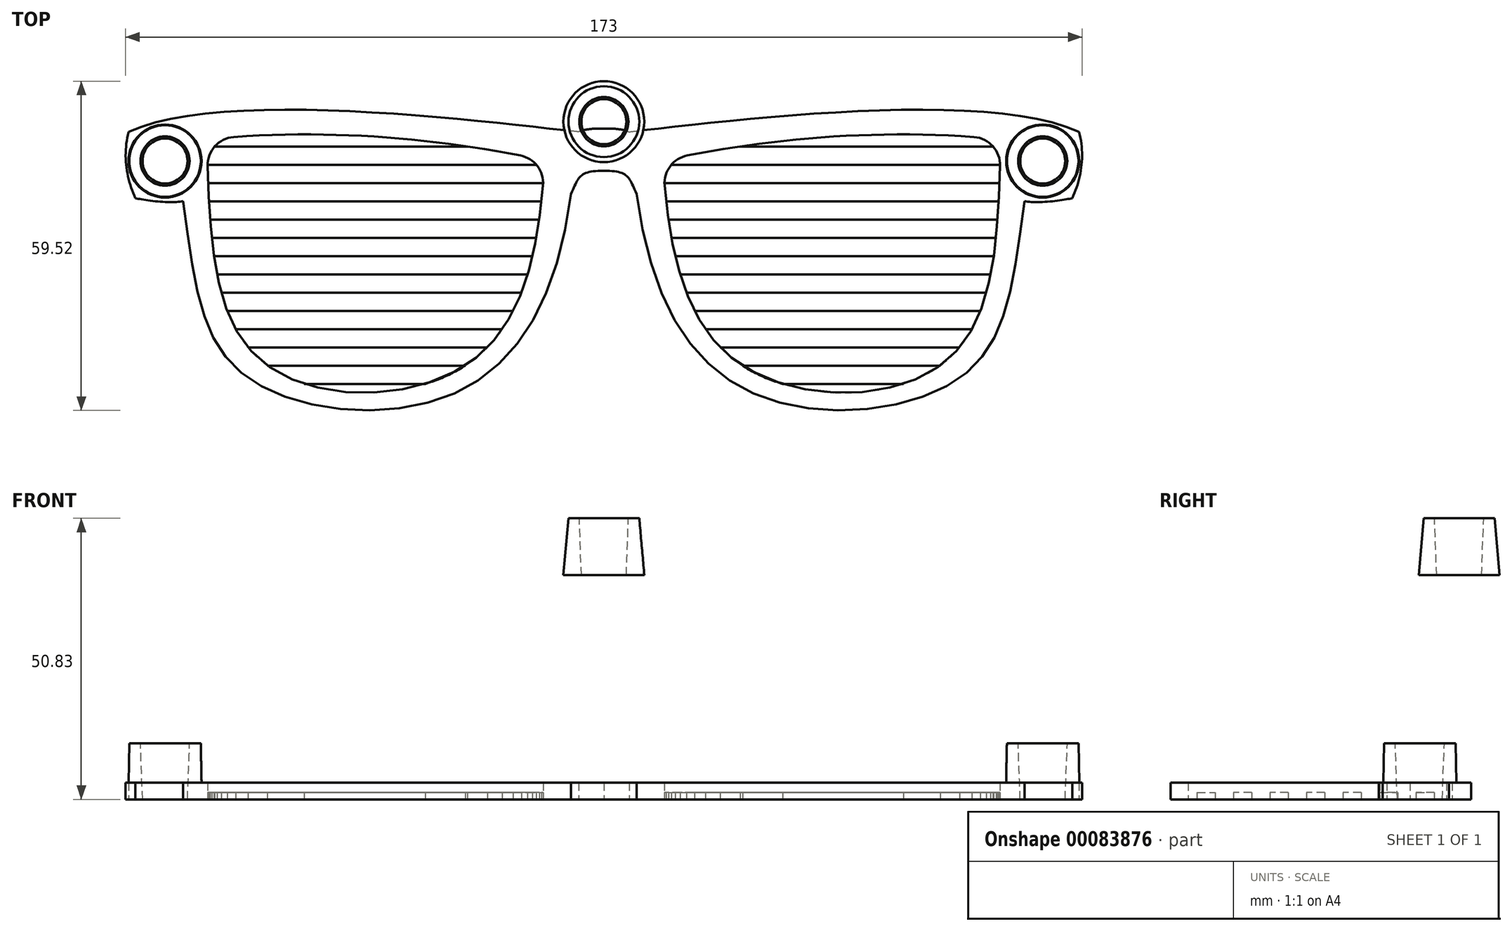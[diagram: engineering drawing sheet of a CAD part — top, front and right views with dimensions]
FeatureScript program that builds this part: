
annotation { "Feature Type Name" : "Feature", "Feature Type Description" : "" }
export const myFeature = defineFeature(function(context is Context, id is Id, definition is map)
    precondition{}
    {
        {
            var Q0;
            Q0=qCreatedBy(makeId("Top.planeOp"),FACE);
            var sketch = newSketch(context, id + "F0", { "sketchPlane" : qUnion([Q0])});
            skFitSpline(sketch, "E0", {"points": [v(0, -1.25) * mm, v(-4.57, -1.84) * mm], "startDerivative": vector(-4.29, -0.03) * mm, "endDerivative": vector(-4.84, -1.9) * mm});
            skFitSpline(sketch, "E1", {"points": [v(-4.57, -1.84) * mm, v(-85.93, -1.84) * mm], "startDerivative": vector(-55.54, 6.07) * mm, "endDerivative": vector(-50.97, -23.71) * mm});
            skFitSpline(sketch, "E2", {"points": [v(-76.11, -14.35) * mm, v(-64.79, -46.04) * mm, v(-27.62, -49.4) * mm, v(-5.92, -13.06) * mm], "startDerivative": vector(19.74, -143.66) * mm, "endDerivative": vector(20.37, 155.62) * mm});
            skFitSpline(sketch, "E3", {"points": [v(-5.92, -13.06) * mm, v(0, -8.87) * mm], "startDerivative": vector(4.13, 9.55) * mm, "endDerivative": vector(13.05, 0) * mm});
            skLineSegment(sketch, "E4", {"start": v(0, -1.25) * mm, "end": v(0, -8.87) * mm});
            skFitSpline(sketch, "E5", {"points": [v(-85.93, -1.84) * mm, v(-84.72, -13.81) * mm], "startDerivative": vector(-3.44, -12.2) * mm, "endDerivative": vector(4.98, -10.41) * mm});
            skFitSpline(sketch, "E6", {"points": [v(-84.72, -13.81) * mm, v(-76.11, -14.35) * mm], "startDerivative": vector(4.96, -1.42) * mm, "endDerivative": vector(5.45, 1.47) * mm});
            skCircle(sketch, "E7", {"center": v(-79.38, -7.12) * mm, "radius": 4.25 * mm});
            skFitSpline(sketch, "E8", {"points": [v(-10.67, -7.02) * mm, v(-24.61, -43.79) * mm, v(-62.05, -43.18) * mm, v(-71.83, -3.21) * mm], "startDerivative": vector(-7.94, -134.67) * mm, "endDerivative": vector(-5.24, 133.94) * mm});
            skFitSpline(sketch, "E9", {"points": [v(-71.83, -3.21) * mm, v(-10.67, -7.02) * mm], "startDerivative": vector(63.48, 6.5) * mm, "endDerivative": vector(56.84, -12.23) * mm});
            skSolve(sketch);
        }
        {
            var Q0;
            Q0=makeQuery(id+"F0.imprint","IMPRINT",FACE,{"disambiguationData":[TD([[makeQuery(id+"F0.imprint","IMPRINT",EDGE,{"derivedFrom":sQuery(id+"F0.wireOp",EDGE,"E0")}),1.0]])]});
            extrude(context, id + "F1", {"entities" : qUnion([Q0]), "depth" : 3.05 * mm});
        }
        {
            var Q0;
            {var subQ0=sQuery(id+"F0.wireOp",EDGE,"E9");var subQ1=sQuery(id+"F0.wireOp",EDGE,"E8");Q0=makeQuery(id+"F1.opExtrude","SWEPT_EDGE",EDGE,{"disambiguationData":[OSD([subQ1,subQ0]),TDD([makeQuery(id+"F0.imprint","INTERSECT",VERTEX,{"disambiguationData":[OD(1.0)],"derivedFrom":[subQ1,subQ0]})])]});}
            var Q1;
            {var subQ0=sQuery(id+"F0.wireOp",EDGE,"E9");var subQ1=sQuery(id+"F0.wireOp",EDGE,"E8");Q1=makeQuery(id+"F1.opExtrude","SWEPT_EDGE",EDGE,{"disambiguationData":[OSD([subQ1,subQ0]),TDD([makeQuery(id+"F0.imprint","INTERSECT",VERTEX,{"disambiguationData":[OD(0.0)],"derivedFrom":[subQ1,subQ0]})])]});}
            fillet(context, id + "F2", {"entities" : qUnion([Q0, Q1]), "radius" : 5.08 * mm, "tangentPropagation" : true, "allowEdgeOverflow" : false});
        }
        {
            var Q0;
            Q0=qCreatedBy(makeId("Top.planeOp"),FACE);
            var sketch = newSketch(context, id + "F3", { "sketchPlane" : qUnion([Q0])});
            skLineSegment(sketch, "E10.bottom", {"start": v(-72.86, -4.48) * mm, "end": v(-7.58, -4.48) * mm});
            skLineSegment(sketch, "E10.top", {"start": v(-72.86, -7.78) * mm, "end": v(-7.58, -7.78) * mm});
            skLineSegment(sketch, "E10.left", {"start": v(-72.86, -4.48) * mm, "end": v(-72.86, -7.78) * mm});
            skLineSegment(sketch, "E10.right", {"start": v(-7.58, -4.48) * mm, "end": v(-7.58, -7.78) * mm});
            skLineSegment(sketch, "E11.bottom", {"start": v(-73.3, -11.08) * mm, "end": v(-9.13, -11.08) * mm});
            skLineSegment(sketch, "E11.top", {"start": v(-73.3, -14.39) * mm, "end": v(-9.13, -14.39) * mm});
            skLineSegment(sketch, "E11.left", {"start": v(-73.3, -11.08) * mm, "end": v(-73.3, -14.39) * mm});
            skLineSegment(sketch, "E11.right", {"start": v(-9.13, -11.08) * mm, "end": v(-9.13, -14.39) * mm});
            skLineSegment(sketch, "E12.bottom", {"start": v(-10.38, -17.69) * mm, "end": v(-73, -17.69) * mm});
            skLineSegment(sketch, "E12.top", {"start": v(-10.38, -21) * mm, "end": v(-73, -21) * mm});
            skLineSegment(sketch, "E12.left", {"start": v(-10.38, -17.69) * mm, "end": v(-10.38, -21) * mm});
            skLineSegment(sketch, "E12.right", {"start": v(-73, -17.69) * mm, "end": v(-73, -21) * mm});
            skLineSegment(sketch, "E13.bottom", {"start": v(-11.59, -24.3) * mm, "end": v(-71.88, -24.3) * mm});
            skLineSegment(sketch, "E13.top", {"start": v(-11.59, -27.6) * mm, "end": v(-71.88, -27.6) * mm});
            skLineSegment(sketch, "E13.left", {"start": v(-11.59, -24.3) * mm, "end": v(-11.59, -27.6) * mm});
            skLineSegment(sketch, "E13.right", {"start": v(-71.88, -24.3) * mm, "end": v(-71.88, -27.6) * mm});
            skLineSegment(sketch, "E14.bottom", {"start": v(-13.43, -30.9) * mm, "end": v(-70.24, -30.9) * mm});
            skLineSegment(sketch, "E14.top", {"start": v(-13.43, -34.2) * mm, "end": v(-70.24, -34.2) * mm});
            skLineSegment(sketch, "E14.left", {"start": v(-13.43, -30.9) * mm, "end": v(-13.43, -34.2) * mm});
            skLineSegment(sketch, "E14.right", {"start": v(-70.24, -30.9) * mm, "end": v(-70.24, -34.2) * mm});
            skLineSegment(sketch, "E15.bottom", {"start": v(-17.26, -37.5) * mm, "end": v(-68.12, -37.5) * mm});
            skLineSegment(sketch, "E15.top", {"start": v(-17.26, -40.8) * mm, "end": v(-68.12, -40.8) * mm});
            skLineSegment(sketch, "E15.left", {"start": v(-17.26, -37.5) * mm, "end": v(-17.26, -40.8) * mm});
            skLineSegment(sketch, "E15.right", {"start": v(-68.12, -37.5) * mm, "end": v(-68.12, -40.8) * mm});
            skLineSegment(sketch, "E16.bottom", {"start": v(-61.73, -44.1) * mm, "end": v(-24.35, -44.1) * mm});
            skLineSegment(sketch, "E16.top", {"start": v(-61.73, -47.4) * mm, "end": v(-24.35, -47.4) * mm});
            skLineSegment(sketch, "E16.left", {"start": v(-61.73, -44.1) * mm, "end": v(-61.73, -47.4) * mm});
            skLineSegment(sketch, "E16.right", {"start": v(-24.35, -44.1) * mm, "end": v(-24.35, -47.4) * mm});
            skSolve(sketch);
        }
        {
            var Q0;
            Q0 = qSketchRegion(id + "F3", true);
            extrude(context, id + "F4", {"entities" : qUnion([Q0]), "operationType" : NewBodyOperationType.ADD, "depth" : 1.27 * mm});
        }
        {
            var Q0;
            Q0=qCreatedBy(makeId("Top.planeOp"),FACE);
            var sketch = newSketch(context, id + "F5", { "sketchPlane" : qUnion([Q0])});
            skPoint(sketch, "E17", {"position": v(-79.38, -7.12) * mm});
            skSolve(sketch);
        }
        {
            var Q0;
            Q0=qCreatedBy(makeId("Front.planeOp"),FACE);
            var Q1;
            Q1=sQuery(id+"F5.wireOp",VERTEX,"E17");
            cPlane(context, id + "F6", {"entities" : qUnion([Q0, Q1]), "cplaneType" : CPlaneType.PLANE_POINT, "offset" : 152.4 * mm, "width" : 152.4 * mm, "height" : 152.4 * mm});
        }
        {
            var Q0;
            Q0=qCreatedBy(id+"F6.planeOp",FACE);
            var sketch = newSketch(context, id + "F7", { "sketchPlane" : qUnion([Q0])});
            skLineSegment(sketch, "E18", {"start": v(-79.38, 11.21) * mm, "end": v(-79.38, -6.37) * mm, "construction": true});
            skSolve(sketch);
        }
        {
            var Q0;
            Q0=qCreatedBy(id+"F6.planeOp",FACE);
            var sketch = newSketch(context, id + "F8", { "sketchPlane" : qUnion([Q0])});
            skLineSegment(sketch, "E19", {"start": v(-85.85, 10.16) * mm, "end": v(-83.82, 10.16) * mm});
            skLineSegment(sketch, "E20", {"start": v(-83.82, 10.16) * mm, "end": v(-83.44, 0) * mm});
            skLineSegment(sketch, "E21", {"start": v(-83.44, 0) * mm, "end": v(-86.04, 0) * mm});
            skLineSegment(sketch, "E22", {"start": v(-86.04, 0) * mm, "end": v(-85.85, 10.16) * mm});
            skSolve(sketch);
        }
        {
            var Q0;
            Q0=makeQuery(id+"F8.imprint","IMPRINT",FACE,{"disambiguationData":[TD([[makeQuery(id+"F8.imprint","IMPRINT",EDGE,{"derivedFrom":sQuery(id+"F8.wireOp",EDGE,"E19")}),-1.0]])]});
            var Q1;
            Q1=sQuery(id+"F7.wireOp",EDGE,"E18");
            revolve(context, id + "F9", {"operationType" : NewBodyOperationType.ADD, "entities" : qUnion([Q0]), "axis" : qUnion([Q1]), "revolveType" : RevolveType.FULL});
        }
        {
            var Q0;
            Q0=makeQuery(id+"F1.opExtrude","SWEPT_BODY",BODY,{"disambiguationData":[OSD([sQuery(id+"F0.wireOp",EDGE,"E0"),sQuery(id+"F0.wireOp",EDGE,"E1"),sQuery(id+"F0.wireOp",EDGE,"49ca96db-4137-404c-acfc-dd4352609506"),sQuery(id+"F0.wireOp",EDGE,"E2"),sQuery(id+"F0.wireOp",EDGE,"E3"),sQuery(id+"F0.wireOp",EDGE,"E4")])]});
            var Q1;
            Q1=qCreatedBy(makeId("Right.planeOp"),FACE);
            mirror(context, id + "F10", {"operationType" : NewBodyOperationType.ADD, "entities" : qUnion([Q0]), "mirrorPlane" : qUnion([Q1])});
        }
        {
            var Q0;
            Q0=qCreatedBy(makeId("Front.planeOp"),FACE);
            var sketch = newSketch(context, id + "F11", { "sketchPlane" : qUnion([Q0])});
            skLineSegment(sketch, "E23", {"start": v(4.06, 40.53) * mm, "end": v(7.32, 40.53) * mm});
            skLineSegment(sketch, "E24", {"start": v(7.32, 40.53) * mm, "end": v(6.41, 50.83) * mm});
            skLineSegment(sketch, "E25", {"start": v(6.41, 50.83) * mm, "end": v(4.45, 50.83) * mm});
            skLineSegment(sketch, "E26", {"start": v(4.45, 50.83) * mm, "end": v(4.06, 40.53) * mm});
            skSolve(sketch);
        }
        {
            var Q0;
            Q0=qCreatedBy(makeId("Front.planeOp"),FACE);
            var sketch = newSketch(context, id + "F12", { "sketchPlane" : qUnion([Q0])});
            skLineSegment(sketch, "E27", {"start": v(0, 63.18) * mm, "end": v(0, 29.02) * mm, "construction": true});
            skSolve(sketch);
        }
        {
            var Q0;
            Q0=makeQuery(id+"F11.imprint","IMPRINT",FACE,{"disambiguationData":[TD([[makeQuery(id+"F11.imprint","IMPRINT",EDGE,{"derivedFrom":sQuery(id+"F11.wireOp",EDGE,"E23")}),1.0]])]});
            var Q1;
            Q1=sQuery(id+"F12.wireOp",EDGE,"E27");
            revolve(context, id + "F13", {"entities" : qUnion([Q0]), "axis" : qUnion([Q1]), "revolveType" : RevolveType.FULL});
        }
    });
